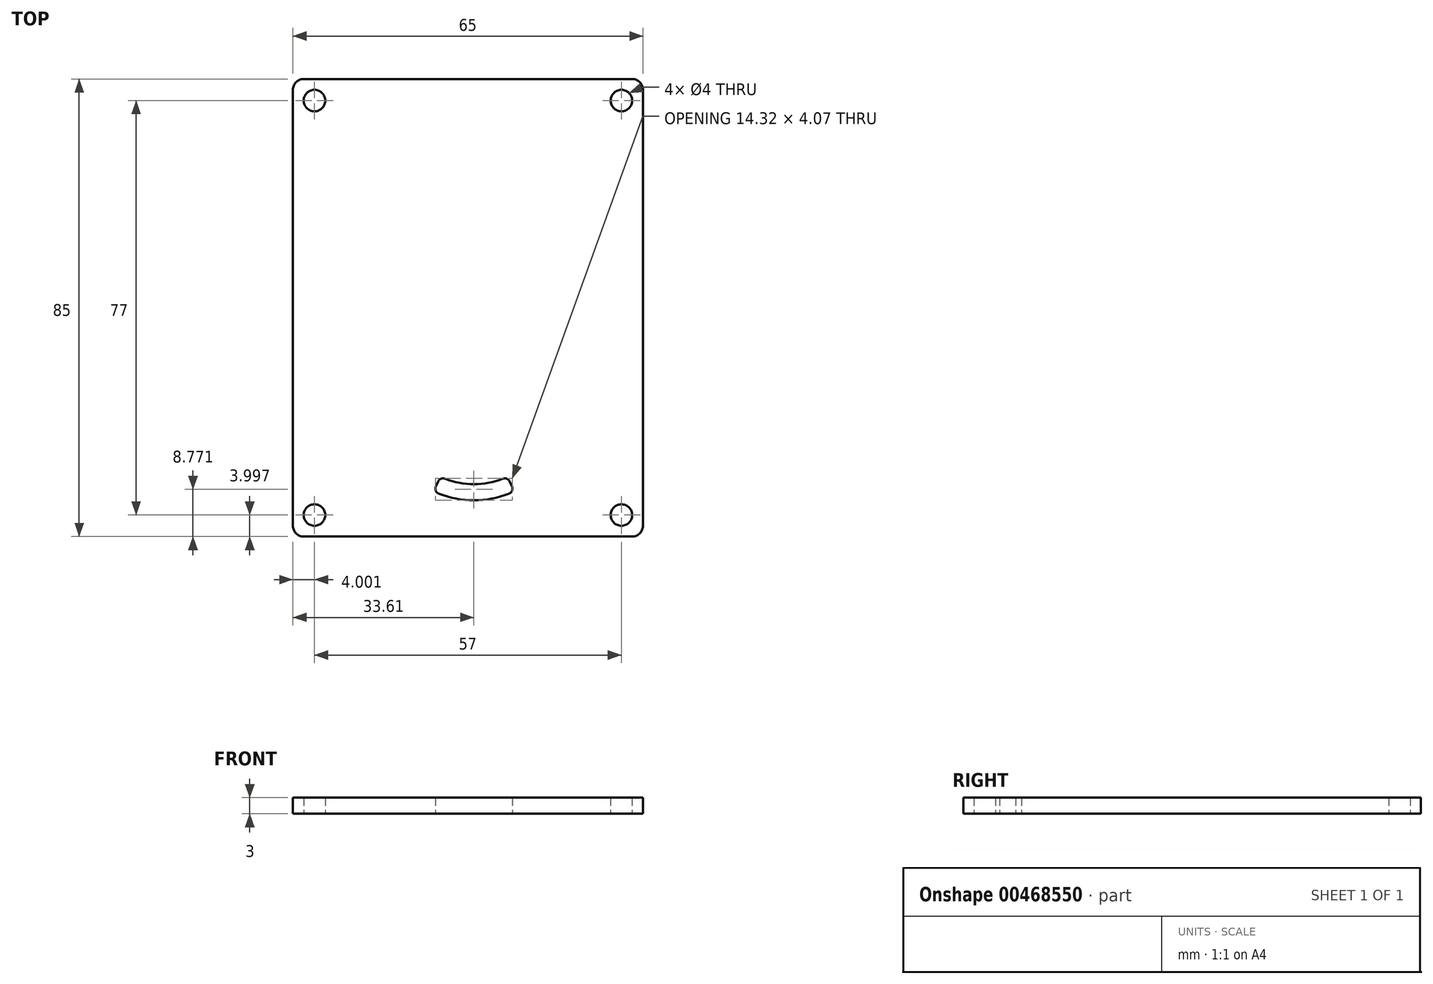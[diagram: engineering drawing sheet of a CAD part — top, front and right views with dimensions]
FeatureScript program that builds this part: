
annotation { "Feature Type Name" : "Feature", "Feature Type Description" : "" }
export const myFeature = defineFeature(function(context is Context, id is Id, definition is map)
    precondition{}
    {
        {
            var Q0;
            Q0=qCreatedBy(makeId("Top.planeOp"),FACE);
            var sketch = newSketch(context, id + "F0", { "sketchPlane" : qUnion([Q0])});
            skLineSegment(sketch, "E0.bottom", {"start": v(-33.6, 36.5) * mm, "end": v(31.4, 36.5) * mm});
            skLineSegment(sketch, "E0.top", {"start": v(-33.6, -48.5) * mm, "end": v(31.4, -48.5) * mm});
            skLineSegment(sketch, "E0.left", {"start": v(-33.6, 36.5) * mm, "end": v(-33.6, -48.5) * mm});
            skLineSegment(sketch, "E0.right", {"start": v(31.4, 36.5) * mm, "end": v(31.4, -48.5) * mm});
            skLineSegment(sketch, "E1", {"start": v(27.4, 36.5) * mm, "end": v(27.4, -48.5) * mm, "construction": true});
            skLineSegment(sketch, "E2", {"start": v(27.4, -48.5) * mm, "end": v(-29.6, -48.5) * mm, "construction": true});
            skLineSegment(sketch, "E3", {"start": v(-29.6, -48.5) * mm, "end": v(-29.6, 36.5) * mm, "construction": true});
            skLineSegment(sketch, "E4", {"start": v(-33.6, 32.5) * mm, "end": v(31.4, 32.5) * mm, "construction": true});
            skLineSegment(sketch, "E5", {"start": v(31.4, -44.5) * mm, "end": v(-33.6, -44.5) * mm, "construction": true});
            skPoint(sketch, "E6", {"position": v(-29.6, 32.5) * mm});
            skPoint(sketch, "E7", {"position": v(27.4, 32.5) * mm});
            skPoint(sketch, "E8", {"position": v(27.4, -44.5) * mm});
            skPoint(sketch, "E9", {"position": v(-29.6, -44.5) * mm});
            skCircle(sketch, "E10", {"center": v(-29.6, -44.5) * mm, "radius": 2 * mm});
            skCircle(sketch, "E11", {"center": v(-29.6, 32.5) * mm, "radius": 2 * mm});
            skCircle(sketch, "E12", {"center": v(27.4, 32.5) * mm, "radius": 2 * mm});
            skCircle(sketch, "E13", {"center": v(27.4, -44.5) * mm, "radius": 2 * mm});
            skLineSegment(sketch, "E14", {"start": v(-33.6, -23.76) * mm, "end": v(31.4, -23.76) * mm, "construction": true});
            skArc(sketch, "E15", {"start": v(-6.25, -37.4) * mm, "mid": v(0, -38.76) * mm, "end": v(6.25, -37.4) * mm});
            skPoint(sketch, "E15.centerSnap0", {"position": v(-1.1, -23.76) * mm});
            skArc(sketch, "E16", {"start": v(-7.5, -40.13) * mm, "mid": v(0, -41.76) * mm, "end": v(7.5, -40.13) * mm});
            skPoint(sketch, "E17", {"position": v(0, -41.76) * mm});
            skPoint(sketch, "E18", {"position": v(7.5, -40.13) * mm});
            skPoint(sketch, "E19", {"position": v(-7.5, -40.13) * mm});
            skLineSegment(sketch, "E20", {"start": v(-6.25, -37.4) * mm, "end": v(-7.5, -40.13) * mm});
            skLineSegment(sketch, "E21", {"start": v(6.25, -37.4) * mm, "end": v(7.5, -40.13) * mm});
            skPoint(sketch, "E22", {"position": v(-6.25, -37.4) * mm});
            skPoint(sketch, "E23", {"position": v(6.25, -37.4) * mm});
            skArc(sketch, "E24.trimOffspring", {"start": v(18, -23.76) * mm, "mid": v(0, -5.76) * mm, "end": v(-18, -23.76) * mm});
            skArc(sketch, "E25.trimOffspring", {"start": v(15, -23.76) * mm, "mid": v(0, -8.76) * mm, "end": v(-15, -23.76) * mm, "construction": true});
            skSolve(sketch);
        }
        {
            var Q0;
            Q0=makeQuery(id+"F0.imprint","IMPRINT",FACE,{"disambiguationData":[TD([[makeQuery(id+"F0.imprint","IMPRINT",EDGE,{"derivedFrom":sQuery(id+"F0.wireOp",EDGE,"E0.bottom")}),-1.0]])]});
            extrude(context, id + "F1", {"entities" : qUnion([Q0]), "depth" : 3 * mm, "offsetDistance" : 25 * mm});
        }
        {
            var Q0;
            Q0=makeQuery(id+"F1.opExtrude","SWEPT_EDGE",EDGE,{"disambiguationData":[OSD([sQuery(id+"F0.wireOp",EDGE,"E0.bottom"),sQuery(id+"F0.wireOp",EDGE,"E0.right")])]});
            var Q1;
            Q1=makeQuery(id+"F1.opExtrude","SWEPT_EDGE",EDGE,{"disambiguationData":[OSD([sQuery(id+"F0.wireOp",EDGE,"E0.top"),sQuery(id+"F0.wireOp",EDGE,"E0.right")])]});
            var Q2;
            Q2=makeQuery(id+"F1.opExtrude","SWEPT_EDGE",EDGE,{"disambiguationData":[OSD([sQuery(id+"F0.wireOp",EDGE,"E0.top"),sQuery(id+"F0.wireOp",EDGE,"E0.left")])]});
            var Q3;
            Q3=makeQuery(id+"F1.opExtrude","SWEPT_EDGE",EDGE,{"disambiguationData":[OSD([sQuery(id+"F0.wireOp",EDGE,"E0.bottom"),sQuery(id+"F0.wireOp",EDGE,"E0.left")])]});
            fillet(context, id + "F2", {"entities" : qUnion([Q0, Q1, Q2, Q3]), "radius" : 2 * mm, "tangentPropagation" : true, "allowEdgeOverflow" : false});
        }
        {
            var Q0;
            Q0=makeQuery(id+"F1.opExtrude","SWEPT_EDGE",EDGE,{"disambiguationData":[OSD([sQuery(id+"F0.wireOp",EDGE,"E16"),sQuery(id+"F0.wireOp",EDGE,"E20")])]});
            var Q1;
            Q1=makeQuery(id+"F1.opExtrude","SWEPT_EDGE",EDGE,{"disambiguationData":[OSD([sQuery(id+"F0.wireOp",EDGE,"E15"),sQuery(id+"F0.wireOp",EDGE,"E20")])]});
            var Q2;
            Q2=makeQuery(id+"F1.opExtrude","SWEPT_EDGE",EDGE,{"disambiguationData":[OSD([sQuery(id+"F0.wireOp",EDGE,"E15"),sQuery(id+"F0.wireOp",EDGE,"E21")])]});
            var Q3;
            Q3=makeQuery(id+"F1.opExtrude","SWEPT_EDGE",EDGE,{"disambiguationData":[OSD([sQuery(id+"F0.wireOp",EDGE,"E16"),sQuery(id+"F0.wireOp",EDGE,"E21")])]});
            fillet(context, id + "F3", {"entities" : qUnion([Q0, Q1, Q2, Q3]), "radius" : 1 * mm, "tangentPropagation" : true, "allowEdgeOverflow" : false});
        }
    });
